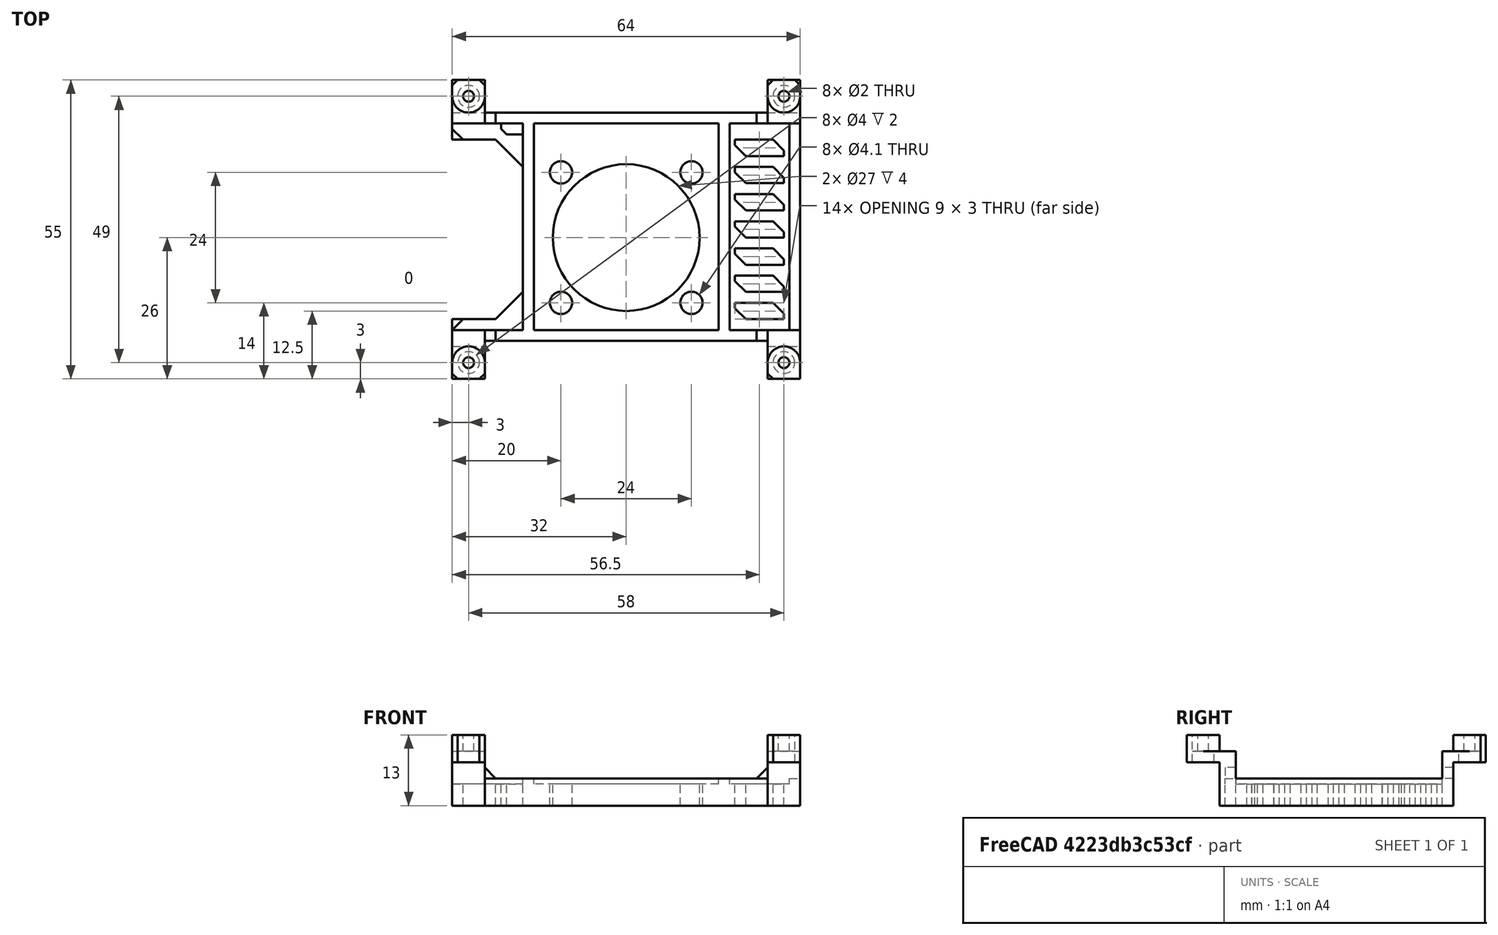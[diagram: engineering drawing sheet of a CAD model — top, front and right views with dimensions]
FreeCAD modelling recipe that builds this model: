
FCSTD DOCUMENT  (FreeCAD 0.18R16146 (Git))
Label: pi-3010-fan-mount
License: All rights reserved
LicenseURL: http://en.wikipedia.org/wiki/All_rights_reserved
objects: Part::Box×27, Part::Cylinder×21, Part::MultiFuse×14, Part::Cut×8, Part::Feature×7, Part::Chamfer×6
note: 83 computed .brp shape members not serialized (recipe doc carries the construction recipe); baked Part::Feature solids carry a one-line shape summary decoded from their .brp

FEATURE [Part::Cylinder] Cylinder
  Angle = 360
  AttacherType = Attacher::AttachEngine3D
  Height = 10
  Placement = pos=(0,49,0) rot=(0,0,1;0rad)
  Radius = 3
FEATURE [Part::Cylinder] Cylinder001
  Angle = 360
  AttacherType = Attacher::AttachEngine3D
  Height = 10
  Placement = pos=(58,0,0) rot=(0,0,1;0rad)
  Radius = 3
FEATURE [Part::Cylinder] Cylinder002
  Angle = 360
  AttacherType = Attacher::AttachEngine3D
  Height = 10
  Placement = pos=(58,49,0) rot=(0,0,1;0rad)
  Radius = 3
FEATURE [Part::Cylinder] Cylinder003
  Angle = 360
  AttacherType = Attacher::AttachEngine3D
  Height = 10
  Radius = 3
FEATURE [Part::Box] Box  label="Cube"
  AttacherType = Attacher::AttachEngine3D
  Height = 10
  Length = 6
  Placement = pos=(-3,-3,0) rot=(0,0,1;0rad)
  Width = 3
FEATURE [Part::Box] Box001  label="Cube001"
  AttacherType = Attacher::AttachEngine3D
  Height = 10
  Length = 6
  Placement = pos=(55,-3,0) rot=(0,0,1;0rad)
  Width = 3
FEATURE [Part::Box] Box002  label="Cube002"
  AttacherType = Attacher::AttachEngine3D
  Height = 10
  Length = 6
  Placement = pos=(55,49,0) rot=(0,0,1;0rad)
  Width = 3
FEATURE [Part::Box] Box003  label="Cube003"
  AttacherType = Attacher::AttachEngine3D
  Height = 10
  Length = 6
  Placement = pos=(-3,49,0) rot=(0,0,1;0rad)
  Width = 3
FEATURE [Part::MultiFuse] Fusion
  Shapes = -> [Box003,Box002,Box001,Box,Cylinder003,Cylinder002,Cylinder001,Cylinder]
FEATURE [Part::Cylinder] Cylinder008
  Angle = 360
  AttacherType = Attacher::AttachEngine3D
  Height = 10
  Placement = pos=(3,3,0) rot=(0,0,1;0rad)
  Radius = 2.05
FEATURE [Part::Cylinder] Cylinder009
  Angle = 360
  AttacherType = Attacher::AttachEngine3D
  Height = 10
  Placement = pos=(27,3,0) rot=(0,0,1;0rad)
  Radius = 2.05
FEATURE [Part::Cylinder] Cylinder010
  Angle = 360
  AttacherType = Attacher::AttachEngine3D
  Height = 10
  Placement = pos=(27,27,0) rot=(0,0,1;0rad)
  Radius = 2.05
FEATURE [Part::Cylinder] Cylinder011
  Angle = 360
  AttacherType = Attacher::AttachEngine3D
  Height = 10
  Placement = pos=(3,27,0) rot=(0,0,1;0rad)
  Radius = 2.05
FEATURE [Part::Box] Box004  label="Cube004"
  AttacherType = Attacher::AttachEngine3D
  Height = 4
  Length = 34
  Placement = pos=(-2,-2,0) rot=(0,0,1;0rad)
  Width = 34
FEATURE [Part::Cylinder] Cylinder012
  Angle = 360
  AttacherType = Attacher::AttachEngine3D
  Height = 10
  Placement = pos=(15,15,0) rot=(0,0,1;0rad)
  Radius = 13.5
FEATURE [Part::MultiFuse] Fusion001
  Shapes = -> [Cylinder012,Cylinder011,Cylinder010,Cylinder009,Cylinder008]
FEATURE [Part::Box] Box006  label="Cube006"
  AttacherType = Attacher::AttachEngine3D
  Height = 5
  Length = 2
  Placement = pos=(59,-3,0) rot=(0,0,1;0rad)
  Width = 55
FEATURE [Part::Box] Box007  label="Cube007"
  AttacherType = Attacher::AttachEngine3D
  Height = 4
  Length = 64
  Placement = pos=(-3,4,0) rot=(0,0,1;0rad)
  Width = 42
FEATURE [Part::Box] Box008  label="Cube008"
  AttacherType = Attacher::AttachEngine3D
  Height = 4
  Length = 34
  Placement = pos=(12,6,0) rot=(0,0,1;0rad)
  Width = 34
FEATURE [Part::Box] Box009  label="Cube009"
  AttacherType = Attacher::AttachEngine3D
  Height = 21
  Length = 15
  Placement = pos=(-4,8,0) rot=(0,0,1;0rad)
  Width = 33
FEATURE [Part::Chamfer] Chamfer
  Base = -> Box009
  Edges = 2 edges r=5: [Edge5,Edge7]
  Placement = pos=(-1,0,0) rot=(0,0,1;0rad)
FEATURE [Part::Box] Box011  label="Cube011"
  AttacherType = Attacher::AttachEngine3D
  Height = 5
  Length = 2
  Placement = pos=(10,4,0) rot=(0,0,1;0rad)
  Width = 42
FEATURE [Part::Box] Box012  label="Cube012"
  AttacherType = Attacher::AttachEngine3D
  Height = 5
  Length = 64
  Placement = pos=(-3,4,0) rot=(0,0,1;0rad)
  Width = 2
FEATURE [Part::Box] Box014  label="Cube014"
  AttacherType = Attacher::AttachEngine3D
  Height = 5
  Length = 2
  Placement = pos=(46,4,0) rot=(0,0,1;0rad)
  Width = 42
FEATURE [Part::Box] Box015  label="Cube015"
  AttacherType = Attacher::AttachEngine3D
  Height = 10
  Length = 9
  Placement = pos=(49,7,0) rot=(0,0,1;0rad)
  Width = 3
FEATURE [Part::Chamfer] Chamfer003009
  Base = -> Box015
  Edges = 2 edges r=2: [Edge1,Edge7]
FEATURE [Part::Feature] Chamfer003009001  label="Chamfer003010"
  Placement = pos=(0,5,0) rot=(0,0,1;0rad)
  shape: bbox 9 x 3 x 10 mm, 8 faces (baked)
FEATURE [Part::Feature] Chamfer003009002  label="Chamfer003011"
  Placement = pos=(0,10,0) rot=(0,0,1;0rad)
  shape: bbox 9 x 3 x 10 mm, 8 faces (baked)
FEATURE [Part::Feature] Chamfer003009003  label="Chamfer003012"
  Placement = pos=(0,15,0) rot=(0,0,1;0rad)
  shape: bbox 9 x 3 x 10 mm, 8 faces (baked)
FEATURE [Part::Feature] Chamfer003009004  label="Chamfer003013"
  Placement = pos=(0,20,0) rot=(0,0,1;0rad)
  shape: bbox 9 x 3 x 10 mm, 8 faces (baked)
FEATURE [Part::Feature] Chamfer003009005  label="Chamfer003014"
  Placement = pos=(0,25,0) rot=(0,0,1;0rad)
  shape: bbox 9 x 3 x 10 mm, 8 faces (baked)
FEATURE [Part::Feature] Chamfer003009006  label="Chamfer003015"
  Placement = pos=(0,30,0) rot=(0,0,1;0rad)
  shape: bbox 9 x 3 x 10 mm, 8 faces (baked)
FEATURE [Part::Cut] Cut
  Base = -> Box004
  Placement = pos=(14,8,0) rot=(0,0,1;0rad)
  Tool = -> Fusion001
FEATURE [Part::Cylinder] Cylinder013
  Angle = 360
  AttacherType = Attacher::AttachEngine3D
  Height = 10
  Placement = pos=(0,49,0) rot=(0,0,1;0rad)
  Radius = 2
FEATURE [Part::Cylinder] Cylinder014
  Angle = 360
  AttacherType = Attacher::AttachEngine3D
  Height = 10
  Placement = pos=(58,0,0) rot=(0,0,1;0rad)
  Radius = 2
FEATURE [Part::Cylinder] Cylinder015
  Angle = 360
  AttacherType = Attacher::AttachEngine3D
  Height = 10
  Placement = pos=(58,49,0) rot=(0,0,1;0rad)
  Radius = 2
FEATURE [Part::Cylinder] Cylinder016
  Angle = 360
  AttacherType = Attacher::AttachEngine3D
  Height = 10
  Radius = 2
FEATURE [Part::Box] Box016  label="Cube016"
  AttacherType = Attacher::AttachEngine3D
  Height = 8
  Length = 6
  Placement = pos=(-3,-3,0) rot=(0,0,1;0rad)
  Width = 6
FEATURE [Part::Box] Box018  label="Cube018"
  AttacherType = Attacher::AttachEngine3D
  Height = 8
  Length = 6
  Placement = pos=(-3,46,0) rot=(0,0,1;0rad)
  Width = 6
FEATURE [Part::Box] Box019  label="Cube019"
  AttacherType = Attacher::AttachEngine3D
  Height = 8
  Length = 6
  Placement = pos=(55,46,0) rot=(0,0,1;0rad)
  Width = 6
FEATURE [Part::Box] Box020  label="Cube020"
  AttacherType = Attacher::AttachEngine3D
  Height = 8
  Length = 6
  Placement = pos=(55,-3,0) rot=(0,0,1;0rad)
  Width = 6
FEATURE [Part::Box] Box021  label="Cube021"
  AttacherType = Attacher::AttachEngine3D
  Height = 10
  Length = 6
  Placement = pos=(-3,-3,0) rot=(0,0,1;0rad)
  Width = 9
FEATURE [Part::Box] Box022  label="Cube022"
  AttacherType = Attacher::AttachEngine3D
  Height = 10
  Length = 6
  Placement = pos=(55,-3,0) rot=(0,0,1;0rad)
  Width = 9
FEATURE [Part::Box] Box023  label="Cube023"
  AttacherType = Attacher::AttachEngine3D
  Height = 10
  Length = 6
  Placement = pos=(55,44,0) rot=(0,0,1;0rad)
  Width = 8
FEATURE [Part::Box] Box024  label="Cube024"
  AttacherType = Attacher::AttachEngine3D
  Height = 10
  Length = 6
  Placement = pos=(-3,44,0) rot=(0,0,1;0rad)
  Width = 8
FEATURE [Part::Box] Box026  label="Cube026"
  AttacherType = Attacher::AttachEngine3D
  Height = 5
  Length = 64
  Placement = pos=(-3,44,0) rot=(0,0,1;0rad)
  Width = 2
FEATURE [Part::MultiFuse] Fusion010
  Placement = pos=(0,1,0) rot=(0,0,1;0rad)
  Shapes = -> [Chamfer003009,Chamfer003009001,Chamfer003009002,Chamfer003009003,Chamfer003009004,Chamfer003009005,Chamfer003009006]
FEATURE [Part::Box] Box027  label="Cube027"
  AttacherType = Attacher::AttachEngine3D
  Height = 10
  Length = 4
  Placement = pos=(6,42,0) rot=(0,0,1;0rad)
  Width = 2
FEATURE [Part::Chamfer] Chamfer003009009
  Base = -> Box027
  Edges = 1 edges r=1: [Edge1]
FEATURE [Part::Cut] Cut001
  Base = -> Box007
  Tool = -> Box008
FEATURE [Part::MultiFuse] Fusion011003
  Shapes = -> [Cut001,Cut]
FEATURE [Part::Cut] Cut002
  Base = -> Fusion011003
  Tool = -> Chamfer
FEATURE [Part::MultiFuse] Fusion011004
  Shapes = -> [Box006,Box012,Box011,Box014,Box026]
FEATURE [Part::Cut] Cut003
  Base = -> Cut002
  Tool = -> Fusion010
FEATURE [Part::Cut] Cut004
  Base = -> Cut003
  Tool = -> Chamfer003009009
FEATURE [Part::MultiFuse] Fusion011005
  Shapes = -> [Cut004,Fusion011004]
FEATURE [Part::MultiFuse] Fusion011006
  Shapes = -> [Box021,Box022,Box023,Box024]
FEATURE [Part::MultiFuse] Fusion011007
  Shapes = -> [Fusion011006,Fusion011005,Fusion]
FEATURE [Part::MultiFuse] Fusion011008
  Shapes = -> [Box016,Box019,Box020,Box018]
FEATURE [Part::Cut] Cut005
  Base = -> Fusion011007
  Tool = -> Fusion011008
FEATURE [Part::Cylinder] Cylinder017
  Angle = 360
  AttacherType = Attacher::AttachEngine3D
  Height = 3
  Placement = pos=(0,49,0) rot=(0,0,1;0rad)
  Radius = 3
FEATURE [Part::Cylinder] Cylinder018
  Angle = 360
  AttacherType = Attacher::AttachEngine3D
  Height = 3
  Radius = 3
FEATURE [Part::Cylinder] Cylinder019
  Angle = 360
  AttacherType = Attacher::AttachEngine3D
  Height = 3
  Placement = pos=(58,49,0) rot=(0,0,1;0rad)
  Radius = 3
FEATURE [Part::Cylinder] Cylinder020
  Angle = 360
  AttacherType = Attacher::AttachEngine3D
  Height = 3
  Placement = pos=(58,0,0) rot=(0,0,1;0rad)
  Radius = 3
FEATURE [Part::MultiFuse] Fusion011009
  Placement = pos=(0,0,10) rot=(0,0,1;0rad)
  Shapes = -> [Cylinder020,Cylinder019,Cylinder018,Cylinder017]
FEATURE [Part::Box] Box028  label="Cube028"
  AttacherType = Attacher::AttachEngine3D
  Height = 3
  Length = 6
  Placement = pos=(-3,-3,10) rot=(0,0,1;0rad)
  Width = 3
FEATURE [Part::Box] Box029  label="Cube029"
  AttacherType = Attacher::AttachEngine3D
  Height = 3
  Length = 6
  Placement = pos=(55,-3,10) rot=(0,0,1;0rad)
  Width = 3
FEATURE [Part::Box] Box030  label="Cube030"
  AttacherType = Attacher::AttachEngine3D
  Height = 3
  Length = 6
  Placement = pos=(55,49,10) rot=(0,0,1;0rad)
  Width = 3
FEATURE [Part::Box] Box031  label="Cube031"
  AttacherType = Attacher::AttachEngine3D
  Height = 3
  Length = 6
  Placement = pos=(-3,49,10) rot=(0,0,1;0rad)
  Width = 3
FEATURE [Part::MultiFuse] Fusion011010
  Shapes = -> [Box031,Box030,Box029,Box028]
FEATURE [Part::MultiFuse] Fusion011011
  Shapes = -> [Fusion011010,Fusion011009,Cut005]
FEATURE [Part::Cylinder] Cylinder021
  Angle = 360
  AttacherType = Attacher::AttachEngine3D
  Height = 16
  Placement = pos=(0,49,0) rot=(0,0,1;0rad)
  Radius = 1
FEATURE [Part::Cylinder] Cylinder022
  Angle = 360
  AttacherType = Attacher::AttachEngine3D
  Height = 16
  Placement = pos=(58,0,0) rot=(0,0,1;0rad)
  Radius = 1
FEATURE [Part::Cylinder] Cylinder023
  Angle = 360
  AttacherType = Attacher::AttachEngine3D
  Height = 16
  Placement = pos=(58,49,0) rot=(0,0,1;0rad)
  Radius = 1
FEATURE [Part::Cylinder] Cylinder024
  Angle = 360
  AttacherType = Attacher::AttachEngine3D
  Height = 16
  Radius = 1
FEATURE [Part::MultiFuse] Fusion011012
  Shapes = -> [Cylinder024,Cylinder023,Cylinder022,Cylinder021]
FEATURE [Part::Cut] Cut006
  Base = -> Fusion011011
  Tool = -> Fusion011012
FEATURE [Part::MultiFuse] Fusion011013
  Shapes = -> [Cylinder013,Cylinder016,Cylinder014,Cylinder015]
FEATURE [Part::Cut] Cut007
  Base = -> Cut006
  Tool = -> Fusion011013
FEATURE [Part::Feature] Cut007001  label="Cut008"
  shape: bbox 64 x 55 x 13 mm, 115 faces (baked)
FEATURE [Part::Chamfer] Chamfer003009010
  Base = -> Cut007001
  Edges = 2 edges r=1.99: [Edge13,Edge242]
FEATURE [Part::Chamfer] Chamfer003009011
  Base = -> Chamfer003009010
  Edges = 4 edges r=2: [Edge135,Edge153,Edge262,Edge267]
FEATURE [Part::Chamfer] Chamfer003009012
  Base = -> Chamfer003009011
  Edges = 7 edges r=1: [Edge17,Edge41,Edge118,Edge120,Edge199,Edge208,Edge220]
